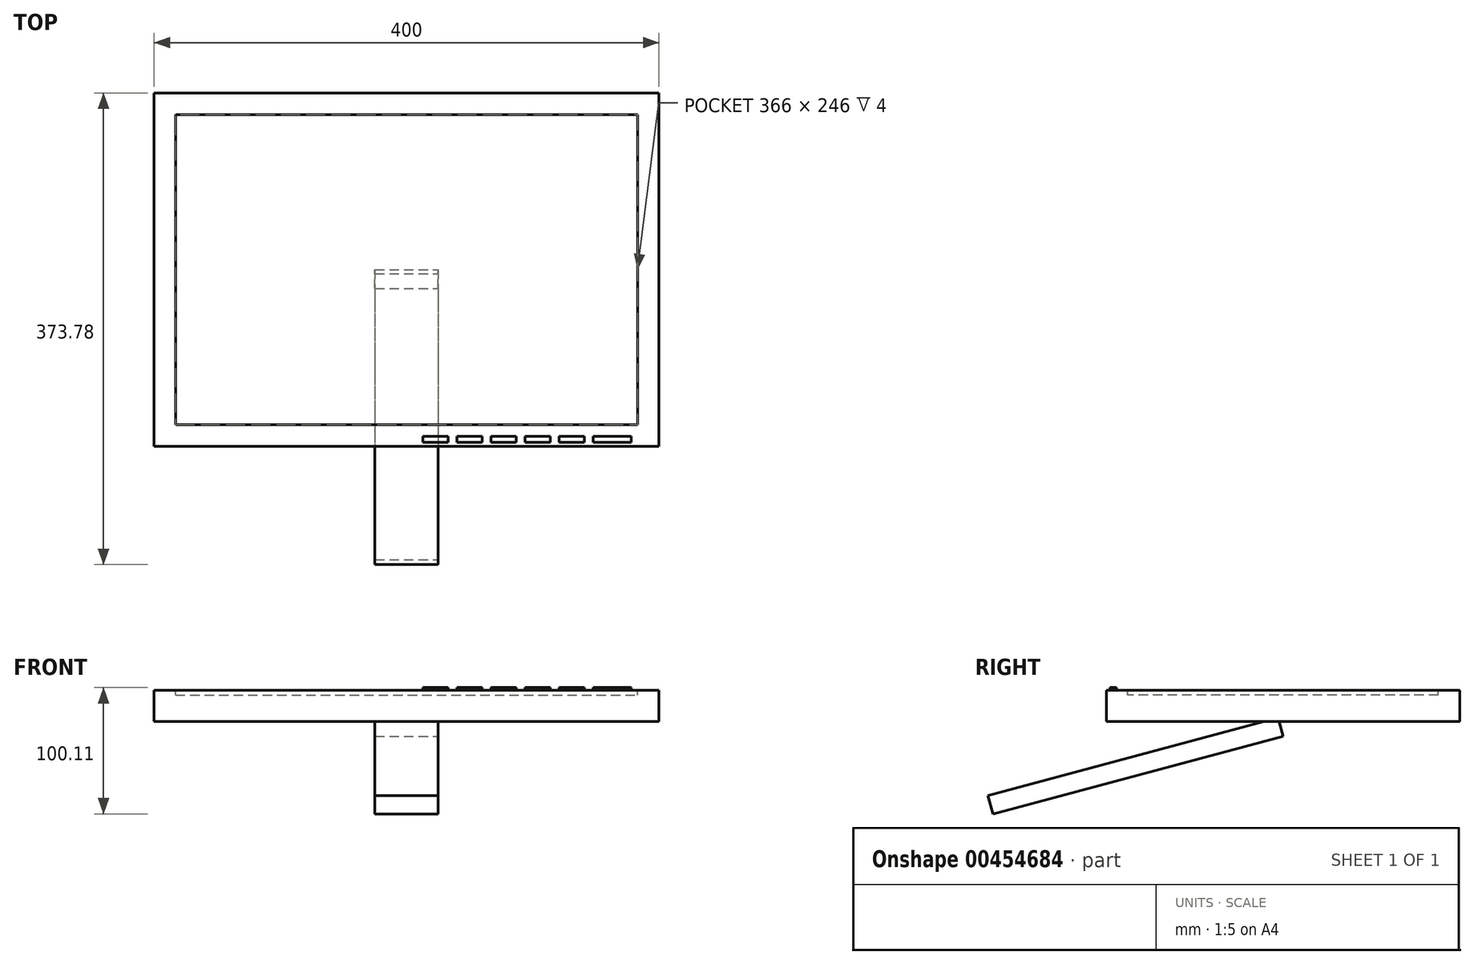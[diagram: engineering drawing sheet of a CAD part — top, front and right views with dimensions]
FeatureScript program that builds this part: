
annotation { "Feature Type Name" : "Feature", "Feature Type Description" : "" }
export const myFeature = defineFeature(function(context is Context, id is Id, definition is map)
    precondition{}
    {
        {
            var Q0;
            Q0=qCreatedBy(makeId("Top.planeOp"),FACE);
            var sketch = newSketch(context, id + "F0", { "sketchPlane" : qUnion([Q0])});
            skLineSegment(sketch, "E0.bottom", {"start": v(-400, 280) * mm, "end": v(0, 280) * mm});
            skLineSegment(sketch, "E0.top", {"start": v(-400, 0) * mm, "end": v(0, 0) * mm});
            skLineSegment(sketch, "E0.left", {"start": v(-400, 280) * mm, "end": v(-400, 0) * mm});
            skLineSegment(sketch, "E0.right", {"start": v(0, 280) * mm, "end": v(0, 0) * mm});
            skSolve(sketch);
        }
        {
            var Q0;
            Q0 = qSketchRegion(id + "F0", true);
            extrude(context, id + "F1", {"entities" : qUnion([Q0]), "depth" : 25 * mm});
        }
        {
            var Q0;
            Q0=makeQuery(id+"F1.opExtrude","CAP_FACE",FACE,{"disambiguationData":[OSD([sQuery(id+"F0.wireOp",EDGE,"E0.bottom"),sQuery(id+"F0.wireOp",EDGE,"E0.top"),sQuery(id+"F0.wireOp",EDGE,"E0.left"),sQuery(id+"F0.wireOp",EDGE,"E0.right")])],"isStart":false});
            var sketch = newSketch(context, id + "F2", { "sketchPlane" : qUnion([Q0])});
            skLineSegment(sketch, "E1.0", {"start": v(-383, 263) * mm, "end": v(-17, 263) * mm});
            skLineSegment(sketch, "E1.1", {"start": v(-383, 263) * mm, "end": v(-383, 17) * mm});
            skLineSegment(sketch, "E1.2", {"start": v(-383, 17) * mm, "end": v(-17, 17) * mm});
            skLineSegment(sketch, "E1.3", {"start": v(-17, 263) * mm, "end": v(-17, 17) * mm});
            skSolve(sketch);
        }
        {
            var Q0;
            Q0 = qSketchRegion(id + "F2", true);
            extrude(context, id + "F3", {"entities" : qUnion([Q0]), "operationType" : NewBodyOperationType.REMOVE, "oppositeDirection" : true, "depth" : 4 * mm});
        }
        {
            var Q0;
            Q0=makeQuery(id+"F1.opExtrude","CAP_FACE",FACE,{"disambiguationData":[OSD([sQuery(id+"F0.wireOp",EDGE,"E0.bottom"),sQuery(id+"F0.wireOp",EDGE,"E0.top"),sQuery(id+"F0.wireOp",EDGE,"E0.left"),sQuery(id+"F0.wireOp",EDGE,"E0.right")])],"isStart":false});
            var sketch = newSketch(context, id + "F4", { "sketchPlane" : qUnion([Q0])});
            skLineSegment(sketch, "E2", {"start": v(-22, 0) * mm, "end": v(-22, 3) * mm});
            skLineSegment(sketch, "E3", {"start": v(-22, 3) * mm, "end": v(-22, 8) * mm});
            skLineSegment(sketch, "E4", {"start": v(-22, 8) * mm, "end": v(0, 8) * mm});
            skLineSegment(sketch, "E5", {"start": v(-22, 8) * mm, "end": v(-52, 8) * mm});
            skLineSegment(sketch, "E6", {"start": v(-52, 8) * mm, "end": v(-52, 3) * mm});
            skLineSegment(sketch, "E7", {"start": v(-52, 3) * mm, "end": v(-22, 3) * mm});
            skLineSegment(sketch, "E8", {"start": v(-52, 8) * mm, "end": v(-59, 8) * mm});
            skLineSegment(sketch, "E9", {"start": v(-59, 8) * mm, "end": v(-79, 8) * mm});
            skLineSegment(sketch, "E10", {"start": v(-79, 8) * mm, "end": v(-79, 3) * mm});
            skLineSegment(sketch, "E11", {"start": v(-79, 3) * mm, "end": v(-59, 3) * mm});
            skLineSegment(sketch, "E12", {"start": v(-59, 3) * mm, "end": v(-59, 8) * mm});
            skLineSegment(sketch, "E13", {"start": v(-79, 8) * mm, "end": v(-86, 8) * mm});
            skLineSegment(sketch, "E14", {"start": v(-86, 8) * mm, "end": v(-86, 3) * mm});
            skLineSegment(sketch, "E15", {"start": v(-86, 3) * mm, "end": v(-106, 3) * mm});
            skLineSegment(sketch, "E16", {"start": v(-106, 3) * mm, "end": v(-106, 8) * mm});
            skLineSegment(sketch, "E17", {"start": v(-106, 8) * mm, "end": v(-86, 8) * mm});
            skLineSegment(sketch, "E18", {"start": v(-106, 8) * mm, "end": v(-113, 8) * mm});
            skLineSegment(sketch, "E19", {"start": v(-113, 8) * mm, "end": v(-133, 8) * mm});
            skLineSegment(sketch, "E20", {"start": v(-133, 8) * mm, "end": v(-133, 3) * mm});
            skLineSegment(sketch, "E21", {"start": v(-133, 8) * mm, "end": v(-140, 8) * mm});
            skLineSegment(sketch, "E22", {"start": v(-140, 8) * mm, "end": v(-160, 8) * mm});
            skLineSegment(sketch, "E23", {"start": v(-160, 8) * mm, "end": v(-160, 3) * mm});
            skLineSegment(sketch, "E24", {"start": v(-160, 3) * mm, "end": v(-140, 3) * mm});
            skLineSegment(sketch, "E25", {"start": v(-140, 3) * mm, "end": v(-140, 8) * mm});
            skLineSegment(sketch, "E26", {"start": v(-160, 8) * mm, "end": v(-167, 8) * mm});
            skLineSegment(sketch, "E27", {"start": v(-167, 8) * mm, "end": v(-167, 3) * mm});
            skLineSegment(sketch, "E28", {"start": v(-167, 3) * mm, "end": v(-187, 3) * mm});
            skLineSegment(sketch, "E29", {"start": v(-187, 3) * mm, "end": v(-187, 8) * mm});
            skLineSegment(sketch, "E30", {"start": v(-187, 8) * mm, "end": v(-167, 8) * mm});
            skLineSegment(sketch, "E31", {"start": v(-113, 8) * mm, "end": v(-113, 3) * mm});
            skLineSegment(sketch, "E32", {"start": v(-113, 3) * mm, "end": v(-133, 3) * mm});
            skSolve(sketch);
        }
        {
            var Q0;
            Q0 = qSketchRegion(id + "F4", true);
            extrude(context, id + "F5", {"entities" : qUnion([Q0]), "operationType" : NewBodyOperationType.ADD, "depth" : 2 * mm});
        }
        {
            var Q0;
            Q0=makeQuery(id+"F1.opExtrude","SWEPT_FACE",FACE,{"disambiguationData":[OSD([sQuery(id+"F0.wireOp",EDGE,"E0.right")])]});
            var sketch = newSketch(context, id + "F6", { "sketchPlane" : qUnion([Q0])});
            skLineSegment(sketch, "E33", {"start": v(0, 0) * mm, "end": v(140, 0) * mm});
            skLineSegment(sketch, "E34", {"start": v(-93.78, -58.62) * mm, "end": v(-89.9, -73.11) * mm});
            skLineSegment(sketch, "E35", {"start": v(-89.9, -73.11) * mm, "end": v(140, -11.5) * mm});
            skLineSegment(sketch, "E36", {"start": v(140, 0) * mm, "end": v(140, -11.5) * mm});
            skLineSegment(sketch, "E37", {"start": v(140, 0) * mm, "end": v(125, 0) * mm});
            skLineSegment(sketch, "E38", {"start": v(125, 0) * mm, "end": v(-93.78, -58.62) * mm});
            skSolve(sketch);
        }
        {
            var Q0;
            Q0 = qSketchRegion(id + "F6", true);
            extrude(context, id + "F7", {"entities" : qUnion([Q0]), "operationType" : NewBodyOperationType.ADD, "oppositeDirection" : true, "depth" : 300 * mm});
        }
        {
            var Q0;
            Q0=makeQuery(id+"F7.opExtrude","SWEPT_FACE",FACE,{"disambiguationData":[OSD([sQuery(id+"F6.wireOp",EDGE,"E35")])]});
            var sketch = newSketch(context, id + "F8", { "sketchPlane" : qUnion([Q0])});
            skLineSegment(sketch, "E39", {"start": v(0, -132.25) * mm, "end": v(-200, -132.25) * mm});
            skPoint(sketch, "E40", {"position": v(-200, -132.25) * mm});
            skLineSegment(sketch, "E41", {"start": v(-200, -132.25) * mm, "end": v(-225, -132.25) * mm});
            skLineSegment(sketch, "E42", {"start": v(-200, -132.25) * mm, "end": v(-175, -132.25) * mm});
            skLineSegment(sketch, "E43", {"start": v(-225, -132.25) * mm, "end": v(-225, 105.76) * mm});
            skLineSegment(sketch, "E44", {"start": v(-225, 105.76) * mm, "end": v(-300, 105.76) * mm});
            skLineSegment(sketch, "E45", {"start": v(-300, 105.76) * mm, "end": v(-300, -132.25) * mm});
            skLineSegment(sketch, "E46", {"start": v(-300, -132.25) * mm, "end": v(-225, -132.25) * mm});
            skLineSegment(sketch, "E47", {"start": v(-175, -132.25) * mm, "end": v(-175, 105.76) * mm});
            skLineSegment(sketch, "E48", {"start": v(-175, 105.76) * mm, "end": v(0, 105.76) * mm});
            skLineSegment(sketch, "E49", {"start": v(0, 105.76) * mm, "end": v(0, -132.25) * mm});
            skSolve(sketch);
        }
        {
            var Q0;
            Q0 = qSketchRegion(id + "F8", true);
            extrude(context, id + "F9", {"entities" : qUnion([Q0]), "operationType" : NewBodyOperationType.REMOVE, "oppositeDirection" : true, "depth" : 15 * mm});
        }
        {
            var Q0;
            Q0=makeQuery(id+"F7.boolean.opBoolean","MERGE",FACE,{"derivedFrom":[makeQuery(id+"F1.opExtrude","SWEPT_FACE",FACE,{"disambiguationData":[OSD([sQuery(id+"F0.wireOp",EDGE,"E0.right")])]}),makeQuery(id+"F7.opExtrude","CAP_FACE",FACE,{"disambiguationData":[OSD([sQuery(id+"F6.wireOp",EDGE,"E34"),sQuery(id+"F6.wireOp",EDGE,"E35"),sQuery(id+"F6.wireOp",EDGE,"E36"),sQuery(id+"F6.wireOp",EDGE,"E37"),sQuery(id+"F6.wireOp",EDGE,"E38")])],"isStart":true})]});
            var sketch = newSketch(context, id + "F10", { "sketchPlane" : qUnion([Q0])});
            skLineSegment(sketch, "E50", {"start": v(140, -11.5) * mm, "end": v(140, 0) * mm});
            skLineSegment(sketch, "E51", {"start": v(140, -11.5) * mm, "end": v(136.92, 0) * mm});
            skLineSegment(sketch, "E52", {"start": v(136.92, 0) * mm, "end": v(140, 0) * mm});
            skSolve(sketch);
        }
        {
            var Q0;
            Q0 = qSketchRegion(id + "F10", true);
            extrude(context, id + "F11", {"entities" : qUnion([Q0]), "operationType" : NewBodyOperationType.REMOVE, "oppositeDirection" : true, "depth" : 300 * mm});
        }
        {
            var Q0;
            Q0=makeQuery(id+"F7.boolean.opBoolean","MERGE",FACE,{"derivedFrom":[makeQuery(id+"F1.opExtrude","SWEPT_FACE",FACE,{"disambiguationData":[OSD([sQuery(id+"F0.wireOp",EDGE,"E0.right")])]}),makeQuery(id+"F7.opExtrude","CAP_FACE",FACE,{"disambiguationData":[OSD([sQuery(id+"F6.wireOp",EDGE,"E34"),sQuery(id+"F6.wireOp",EDGE,"E35"),sQuery(id+"F6.wireOp",EDGE,"E36"),sQuery(id+"F6.wireOp",EDGE,"E37"),sQuery(id+"F6.wireOp",EDGE,"E38")])],"isStart":true})]});
            var sketch = newSketch(context, id + "F12", { "sketchPlane" : qUnion([Q0])});
            skLineSegment(sketch, "E53", {"start": v(125, 0) * mm, "end": v(136.92, 0) * mm});
            skLineSegment(sketch, "E54", {"start": v(136.92, 0) * mm, "end": v(136.12, 2.98) * mm});
            skLineSegment(sketch, "E55", {"start": v(136.12, 2.98) * mm, "end": v(125, 0) * mm});
            skSolve(sketch);
        }
        {
            var Q0;
            Q0 = qSketchRegion(id + "F12", true);
            extrude(context, id + "F13", {"entities" : qUnion([Q0]), "operationType" : NewBodyOperationType.ADD, "oppositeDirection" : true, "depth" : 300 * mm});
        }
    });
